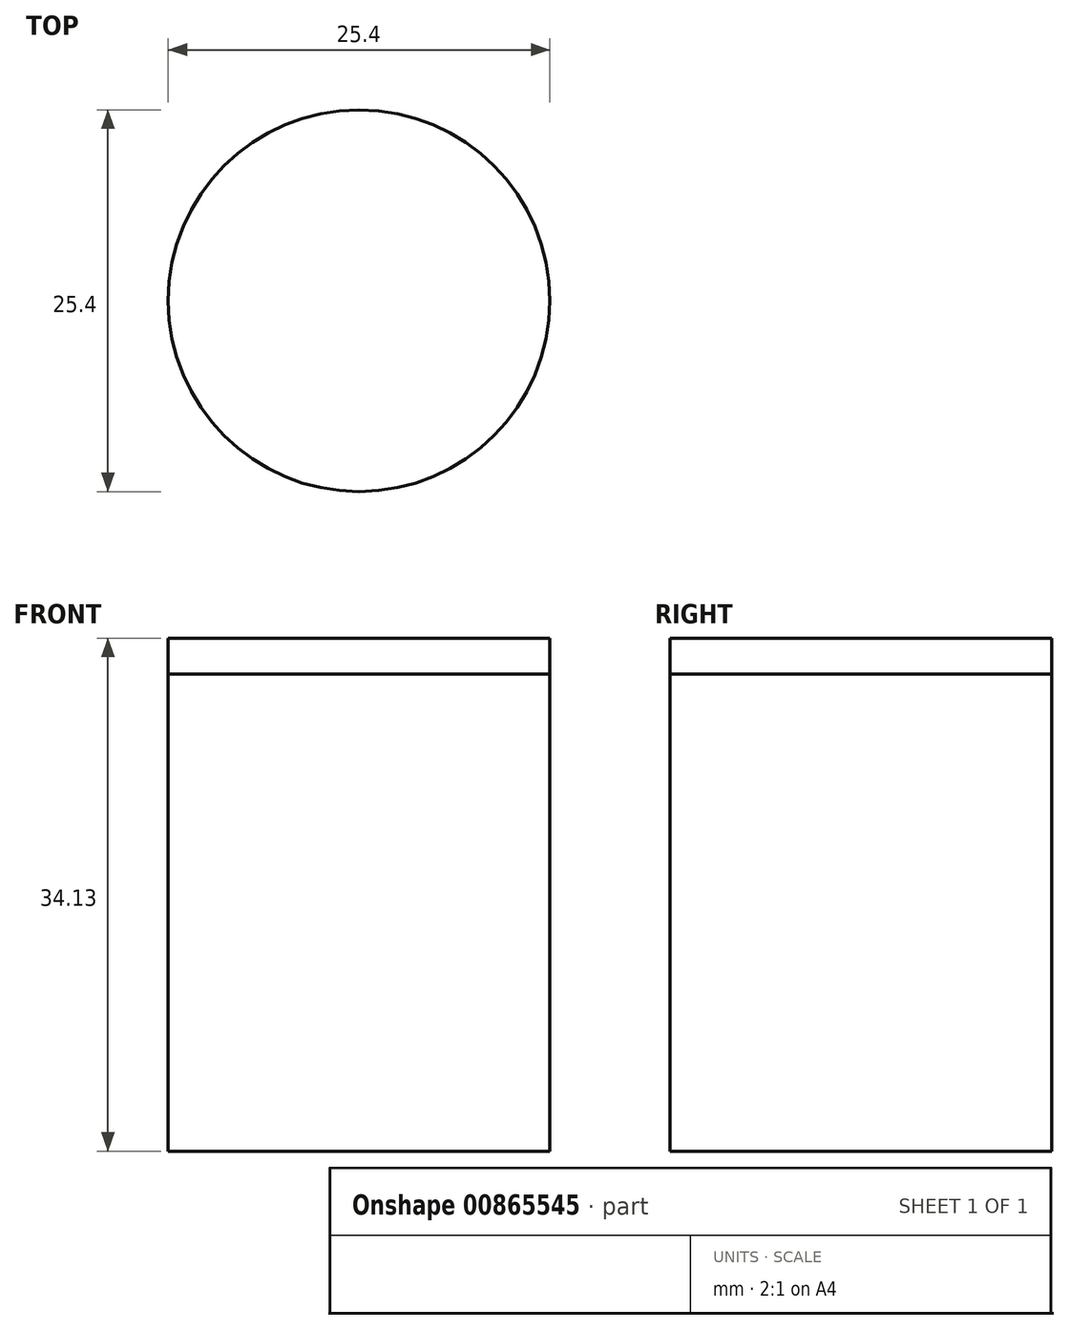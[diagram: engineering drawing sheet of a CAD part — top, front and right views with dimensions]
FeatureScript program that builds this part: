
annotation { "Feature Type Name" : "Feature", "Feature Type Description" : "" }
export const myFeature = defineFeature(function(context is Context, id is Id, definition is map)
    precondition{}
    {
        {
            var Q0;
            Q0=qCreatedBy(makeId("Top.planeOp"),FACE);
            var sketch = newSketch(context, id + "F0", { "sketchPlane" : qUnion([Q0])});
            skCircle(sketch, "E0", {"center": v(0, 0) * mm, "radius": 12.7 * mm});
            skSolve(sketch);
        }
        {
            var Q0;
            Q0=makeQuery(id+"F0.imprint","IMPRINT",FACE,{"disambiguationData":[TD([[makeQuery(id+"F0.imprint","IMPRINT",EDGE,{"derivedFrom":sQuery(id+"F0.wireOp",EDGE,"E0")}),1.0]])]});
            extrude(context, id + "F1", {"entities" : qUnion([Q0]), "depth" : 31.75 * mm, "offsetDistance" : 25.4 * mm});
        }
        {
            var Q0;
            Q0=makeQuery(id+"F1.opExtrude","CAP_FACE",FACE,{"disambiguationData":[OSD([sQuery(id+"F0.wireOp",EDGE,"E0")])],"isStart":false});
            var sketch = newSketch(context, id + "F2", { "sketchPlane" : qUnion([Q0])});
            skCircle(sketch, "E1", {"center": v(0, 0) * mm, "radius": 12.7 * mm});
            skSolve(sketch);
        }
        {
            var Q0;
            Q0 = qSketchRegion(id + "F2", true);
            extrude(context, id + "F3", {"entities" : qUnion([Q0]), "depth" : 2.38 * mm, "offsetDistance" : 25.4 * mm});
        }
    });
